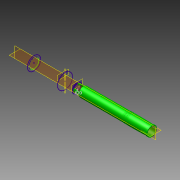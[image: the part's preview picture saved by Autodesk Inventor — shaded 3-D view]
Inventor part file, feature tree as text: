
AUTODESK INVENTOR PART (.ipt)
format: ipt  version: 2015 (Build 190159000, 159)  size: 303,104 bytes
history: native  units: in
note: dims shown in document units (in); Inventor stores cm internally (conversion verified against a paired STEP export)
features: extrude x10, sketch x10, revolve x3, hole x2, plane x2, mirror x1, pattern_circular x1, chamfer x1
ambient origin geometry x8: Origin, YZ Plane, XZ Plane, XY Plane, X Axis, Y Axis, Z Axis, Center Point
bodies: Solid1 (feature_tree)
feature tree (30):
  revolve  "Revolution1"  [1 undecoded]
  extrude  "Extrusion1"  Depth=0.29in
  hole  "Hole1"  [1 undecoded]
  hole  "Hole2"  [1 undecoded]
  sketch  "Sketch3"  dims[d4=0.3in d5=0.1in]
  extrude  "Extrusion2"  Depth=0.3in
  extrude  "Extrusion3"  Depth=0.05in
  extrude  "Extrusion4"  Depth=0.04in
  mirror  "Mirror1"
  plane  "Work Plane2"
  sketch  "Sketch7"  dims[d8=0.3in d9=0.44in]
  extrude  "Extrusion5"  Depth=0.2in TaperAngle=0.0deg
  extrude  "Extrusion6"  Depth=0.125in
  pattern_circular  "Circular Pattern1"  [2 undecoded]
  plane  "Work Plane3"
  extrude  "Extrusion7"  Depth=0.125in TaperAngle=0.0deg
  sketch  "Sketch9"  dims[d12=90.0deg d13=0.04in]
  extrude  "Extrusion8"  Depth=0.125in TaperAngle=0.0deg
  extrude  "Extrusion9"  [1 undecoded]
  revolve  "Revolution2"  [1 undecoded]
  revolve  "Revolution3"  [1 undecoded]
  extrude  "Extrusion10"  Depth=0.125in
  chamfer  "Chamfer1"  Distance=0.01in
  sketch  "Sketch1"  dims[d0=0.07in d1=0.4in]
  sketch  "Sketch2"  dims[d2=0.365in d3=0.29in]
  sketch  "Sketch4"  dims[d6=0.06in d7=0.3in]
  sketch  "Sketch8"  dims[d10=0.28in d11=0.05in]
  sketch  "Sketch10"  dims[d14=0.2in d15=1.0in d16=0.0in]
  sketch  "Sketch11"  dims[d17=1.0in d18=1.0in]
  sketch  "Sketch12"  dims[d19=0.1875in d20=0.75in d21=0.25in d22=0.25in d23=0.5635in d24=0.4375in d25=0.0in d26=1.0in d27=1.0in d28=0.1875in d29=0.75in d30=0.25in d31=0.05in d32=0.5635in d33=0.375in d34=0.0in d35=0.07in d36=0.0in d37=0.085in d38=0.0in d39=1.15in d40=0.0in d42=-1.44in d43=0.45in d44=0.025in d45=0.025in d46=0.01in d47=0.03in d48=0.05in d49=0.0in d50=0.05in d51=0.0in d52=5.1181in d53=360.0deg d55=-1.8in d56=1.8in d57=0.0in d58=0.02in d59=0.4in d60=0.0in d61=0.2in d62=0.0in d63=0.2in d64=0.4466in d65=0.1in d66=30.0deg d67=0.0053in d68=0.0053in d69=0.0053in d70=0.0in d71=0.0053in d72=0.125in d73=45.0deg]
note: 8 required parameter values undecoded (feature->parameter linkage not recoverable at this tier; creation-order binding heuristic only, values carry confidence <= 0.55)